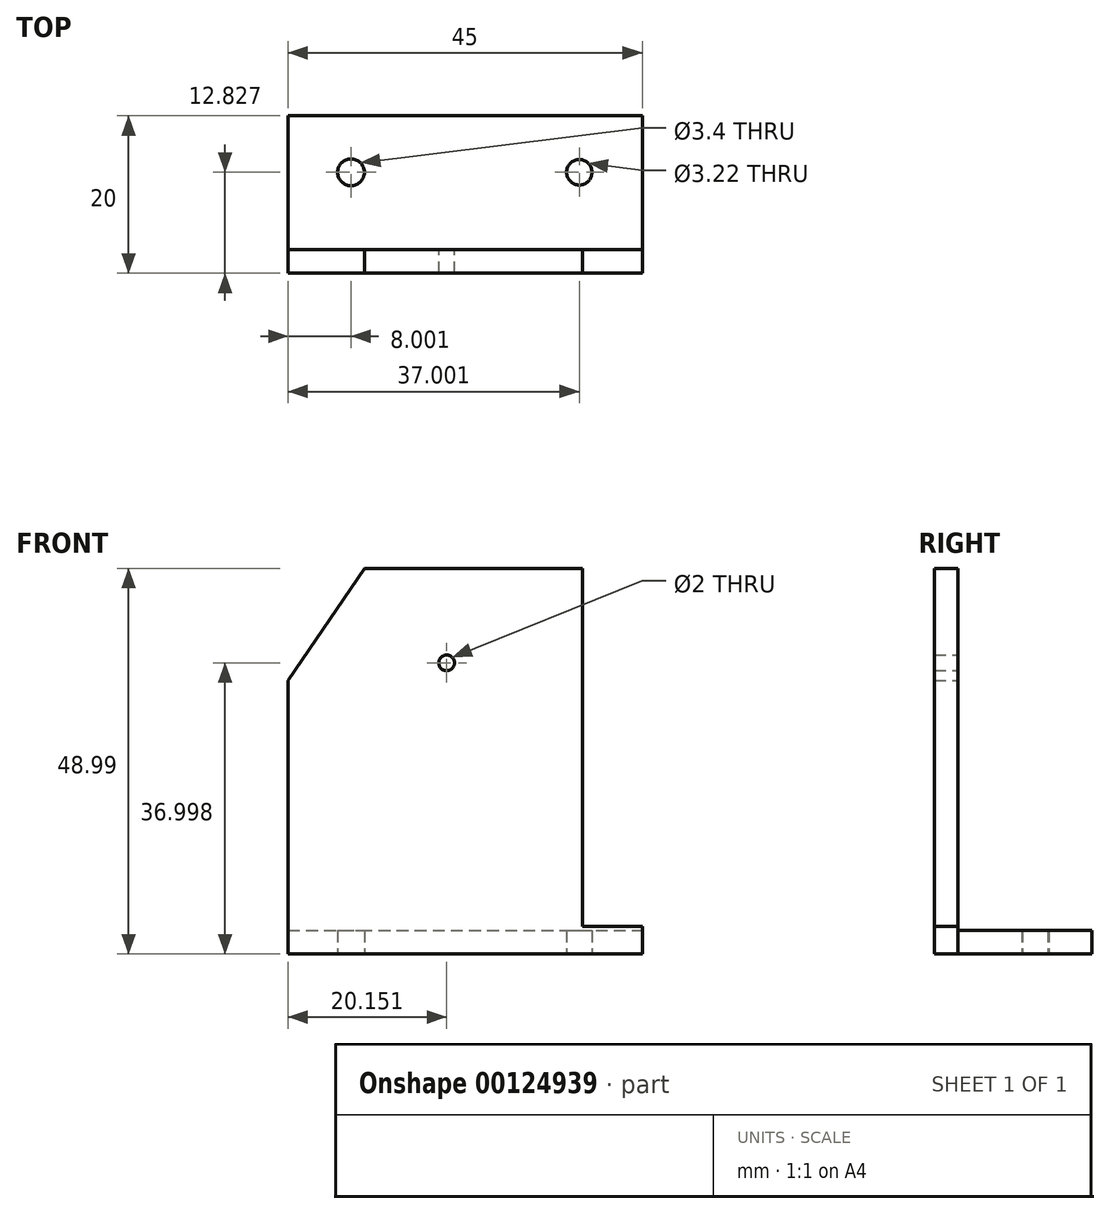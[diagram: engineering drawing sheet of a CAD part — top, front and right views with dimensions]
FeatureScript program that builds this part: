
annotation { "Feature Type Name" : "Feature", "Feature Type Description" : "" }
export const myFeature = defineFeature(function(context is Context, id is Id, definition is map)
    precondition{}
    {
        {
            var Q0;
            Q0=qCreatedBy(makeId("Front.planeOp"),FACE);
            var sketch = newSketch(context, id + "F0", { "sketchPlane" : qUnion([Q0])});
            skLineSegment(sketch, "E0.bottom", {"start": v(-32.87, 11.25) * mm, "end": v(-21.4, 10.36) * mm});
            skLineSegment(sketch, "E0.top", {"start": v(-33.29, 5.9) * mm, "end": v(-21.82, 5.01) * mm});
            skLineSegment(sketch, "E0.left", {"start": v(-32.87, 11.25) * mm, "end": v(-33.29, 5.9) * mm});
            skLineSegment(sketch, "E0.right", {"start": v(-21.4, 10.36) * mm, "end": v(-21.82, 5.01) * mm});
            skCircle(sketch, "E1", {"center": v(-36.58, 8.03) * mm, "radius": 1.23 * mm});
            skLineSegment(sketch, "E2", {"start": v(-21.5, 9.24) * mm, "end": v(-19.71, 9.1) * mm});
            skLineSegment(sketch, "E3", {"start": v(-19.71, 9.1) * mm, "end": v(-19.71, 7.18) * mm});
            skLineSegment(sketch, "E4", {"start": v(-19.71, 7.18) * mm, "end": v(-21.66, 7.09) * mm});
            skCircle(sketch, "E5", {"center": v(-17.91, 7.7) * mm, "radius": 1.15 * mm});
            skLineSegment(sketch, "E6", {"start": v(-37.07, 13.52) * mm, "end": v(-41.14, 9.38) * mm});
            skLineSegment(sketch, "E7", {"start": v(-41.14, 9.38) * mm, "end": v(-41.14, 1.17) * mm});
            skLineSegment(sketch, "E8", {"start": v(-41.14, 1.17) * mm, "end": v(-12.1, 1.17) * mm});
            skLineSegment(sketch, "E9", {"start": v(-12.1, 1.17) * mm, "end": v(-12.1, 9.38) * mm});
            skLineSegment(sketch, "E10", {"start": v(-12.1, 9.38) * mm, "end": v(-16.65, 13.45) * mm});
            skLineSegment(sketch, "E11", {"start": v(-16.65, 13.45) * mm, "end": v(-37.07, 13.52) * mm});
            skLineSegment(sketch, "E12.bottom", {"start": v(-51.3, -18.1) * mm, "end": v(-27.3, -18.1) * mm});
            skLineSegment(sketch, "E12.top", {"start": v(-51.3, -32.1) * mm, "end": v(-27.3, -32.1) * mm});
            skLineSegment(sketch, "E12.left", {"start": v(-51.3, -18.1) * mm, "end": v(-51.3, -32.1) * mm});
            skLineSegment(sketch, "E12.right", {"start": v(-27.3, -18.1) * mm, "end": v(-27.3, -32.1) * mm});
            skLineSegment(sketch, "E13", {"start": v(4.57, -32.1) * mm, "end": v(-59.19, -32.1) * mm, "construction": true});
            skCircle(sketch, "E14", {"center": v(-54.3, -25.1) * mm, "radius": 1 * mm});
            skCircle(sketch, "E15", {"center": v(-24.3, -25.1) * mm, "radius": 1 * mm});
            skPoint(sketch, "E16", {"position": v(-27.3, -25.1) * mm});
            skLineSegment(sketch, "E17", {"start": v(-61.71, -25.1) * mm, "end": v(7.1, -25.1) * mm, "construction": true});
            skLineSegment(sketch, "E18", {"start": v(-64.46, -62.1) * mm, "end": v(-19.46, -62.1) * mm});
            skLineSegment(sketch, "E19", {"start": v(-19.46, -62.1) * mm, "end": v(-19.46, -27.31) * mm});
            skLineSegment(sketch, "E20", {"start": v(-19.46, -27.31) * mm, "end": v(-23.89, -13.1) * mm});
            skLineSegment(sketch, "E21", {"start": v(-23.89, -13.1) * mm, "end": v(-54.73, -13.1) * mm});
            skLineSegment(sketch, "E22", {"start": v(-54.73, -13.1) * mm, "end": v(-64.46, -27.31) * mm});
            skLineSegment(sketch, "E23", {"start": v(-64.46, -27.31) * mm, "end": v(-64.46, -62.1) * mm});
            skPoint(sketch, "E24", {"position": v(-39.3, -32.1) * mm});
            skPoint(sketch, "E25", {"position": v(-39.3, -13.1) * mm});
            skLineSegment(sketch, "E26", {"start": v(-51.3, -22.1) * mm, "end": v(-52.3, -22.1) * mm});
            skLineSegment(sketch, "E27", {"start": v(-52.3, -22.1) * mm, "end": v(-52.3, -28.1) * mm});
            skLineSegment(sketch, "E28", {"start": v(-52.3, -28.1) * mm, "end": v(-51.3, -28.1) * mm});
            skPoint(sketch, "E29", {"position": v(-52.3, -25.1) * mm});
            skCircle(sketch, "E30", {"center": v(-44.3, -25.1) * mm, "radius": 1 * mm});
            skLineSegment(sketch, "E31", {"start": v(-27.07, -13.1) * mm, "end": v(-27.07, -58.6) * mm});
            skLineSegment(sketch, "E32", {"start": v(-27.07, -58.6) * mm, "end": v(-19.46, -58.6) * mm});
            skSolve(sketch);
        }
        {
            var Q0;
            {var subQ4=sQuery(id+"F0.wireOp",EDGE,"E12.bottom");Q0=makeQuery(id+"F0.imprint","IMPRINT",FACE,{"disambiguationData":[TD([[makeQuery(id+"F0.imprint","IMPRINT",EDGE,{"derivedFrom":subQ4}),1.0]])]});}
            var Q1;
            Q1=makeQuery(id+"F0.imprint","IMPRINT",FACE,{"disambiguationData":[TD([[makeQuery(id+"F0.imprint","IMPRINT",EDGE,{"derivedFrom":sQuery(id+"F0.wireOp",EDGE,"E14")}),1.0]])]});
            var Q2;
            {var subQ0=sQuery(id+"F0.wireOp",EDGE,"E26");Q2=makeQuery(id+"F0.imprint","IMPRINT",FACE,{"disambiguationData":[TD([[makeQuery(id+"F0.imprint","IMPRINT",EDGE,{"derivedFrom":subQ0}),1.0]])]});}
            var Q3;
            {var subQ3=sQuery(id+"F0.wireOp",EDGE,"E12.bottom");Q3=makeQuery(id+"F0.imprint","IMPRINT",FACE,{"disambiguationData":[TD([[makeQuery(id+"F0.imprint","IMPRINT",EDGE,{"derivedFrom":subQ3}),-1.0]])]});}
            extrude(context, id + "F1", {"entities" : qUnion([Q0, Q1, Q2, Q3]), "depth" : 3 * mm});
        }
        {
            var Q0;
            Q0=makeQuery(id+"F1.opExtrude","SWEPT_FACE",FACE,{"disambiguationData":[OSD([sQuery(id+"F0.wireOp",EDGE,"E18")])]});
            var sketch = newSketch(context, id + "F2", { "sketchPlane" : qUnion([Q0])});
            skLineSegment(sketch, "E33.bottom", {"start": v(-64.46, 3) * mm, "end": v(-19.46, 3) * mm});
            skLineSegment(sketch, "E33.top", {"start": v(-64.46, -17) * mm, "end": v(-19.46, -17) * mm});
            skLineSegment(sketch, "E33.left", {"start": v(-64.46, 3) * mm, "end": v(-64.46, -17) * mm});
            skLineSegment(sketch, "E33.right", {"start": v(-19.46, 3) * mm, "end": v(-19.46, -17) * mm});
            skCircle(sketch, "E34", {"center": v(-56.46, -9.83) * mm, "radius": 1.7 * mm});
            skCircle(sketch, "E35", {"center": v(-27.46, -9.83) * mm, "radius": 1.61 * mm});
            skPoint(sketch, "E36", {"position": v(-64.46, -7) * mm});
            skSolve(sketch);
        }
        {
            var Q0;
            {var subQ2=sQuery(id+"F2.wireOp",EDGE,"E33.top");Q0=makeQuery(id+"F2.imprint","IMPRINT",FACE,{"disambiguationData":[TD([[makeQuery(id+"F2.imprint","IMPRINT",EDGE,{"derivedFrom":subQ2}),1.0]])]});}
            extrude(context, id + "F3", {"entities" : qUnion([Q0]), "oppositeDirection" : true, "depth" : 3 * mm});
        }
    });
